# Revit family: TSM Betonschraube Sechskantkopf mit angepresster Scheibe, vz
name_source: partatom
category: HLS-Bauteile
units: mm (PartAtom-declared; Revit-internal decimal feet)

## family parameters
Arbeitsebenenbasiert = Ja
Beim Laden mit Abzugskörper schneiden = Nein
Bemaßung runder Anschluss = Durchmesser verwenden
Beschriftungsausrichtung beibehalten = Nein
Gemeinsam genutzt = Ja
Immer vertikal = Nein
Raumberechnungspunkt = Nein
Teiletyp = Normal

## types (4) — shared parameters
Fabrikat = Toge
Firma = MEFA Befestigungs- und Montagesysteme GmbH
Form Kopf = Sechskantkopf
Kurztext1 = Betonschraube TSM
Material = Stahl
Mengeneinheit = St
Oberflaeche = galvanisch verzinkt
Vorgabe-Ansicht = 1219 mm

## per-type parameters (varying)
| type | Artikelnummer | Bohrerdurchmesser | Durchmesser Kopf | EAN | Gewicht | Gewicht pro Bauteil | Innengewindemuffe | Kurztext2 | Länge | Schlüsselweite | max. Klemmstärke | min. Bohrlochtiefe | min. Verankerungstiefe | vpe |
| TSM Betonschraube Sechskantkopf mit angepresster Scheibe, vz  6x60 | 2230663 | 6 mm | 15 mm | 4260116911430 | 0.02 kg | 0.02 kg | Sechskantkopf mit angepresster Scheibe, vz  6x 50 | 6x60 mm Sechskantkopf SW 13 | 60 mm  [stored 0.19685 ft] | 13 | 5 mm  [stored 0.0164042 ft] | 60 mm | 55 mm | 100 |
| TSM Betonschraube Sechskantkopf mit angepresster Scheibe, vz  8x60 | 2230866 | 8 mm | 16 mm | 4250928463630 | 0.03 kg | 0.03 kg | Sechskantkopf mit angepresster Scheibe, vz  8x 60 | 8x60 mm Sechskantkopf SW 13 | 60 mm  [stored 0.19685 ft] | 13 | 5 mm  [stored 0.0164042 ft] | 65 mm | 55 mm | 50 |
| TSM Betonschraube Sechskantkopf mit angepresster Scheibe, vz  8x100 | 2230901 | 8 mm | 16 mm | 4250928449795 | 0.05 kg | 0.05 kg | Sechskantkopf mit angepresster Scheibe, vz  8x100 | 8x100 mm Sechskantkopf SW 13 | 100 mm  [stored 0.328084 ft] | 13 | 35 mm  [stored 0.114829 ft] | 75 mm | 65 mm | 50 |
| TSM Betonschraube Sechskantkopf mit angepresster Scheibe, vz  10x90 | 22310090 | 10 mm | 20 mm | 4260116912628 | 0.07 kg | 0.07 kg | Sechskantkopf mit angepresster Scheibe, vz 10x 85 | 10x90 mm Sechskantkopf SW 15 | 90 mm  [stored 0.295276 ft] | 15 | 5 mm  [stored 0.0164042 ft] | 95 mm | 85 mm | 50 |

note: [stored X ft] marks values corroborated as IEEE doubles in the binary element streams (Revit-internal decimal feet)
